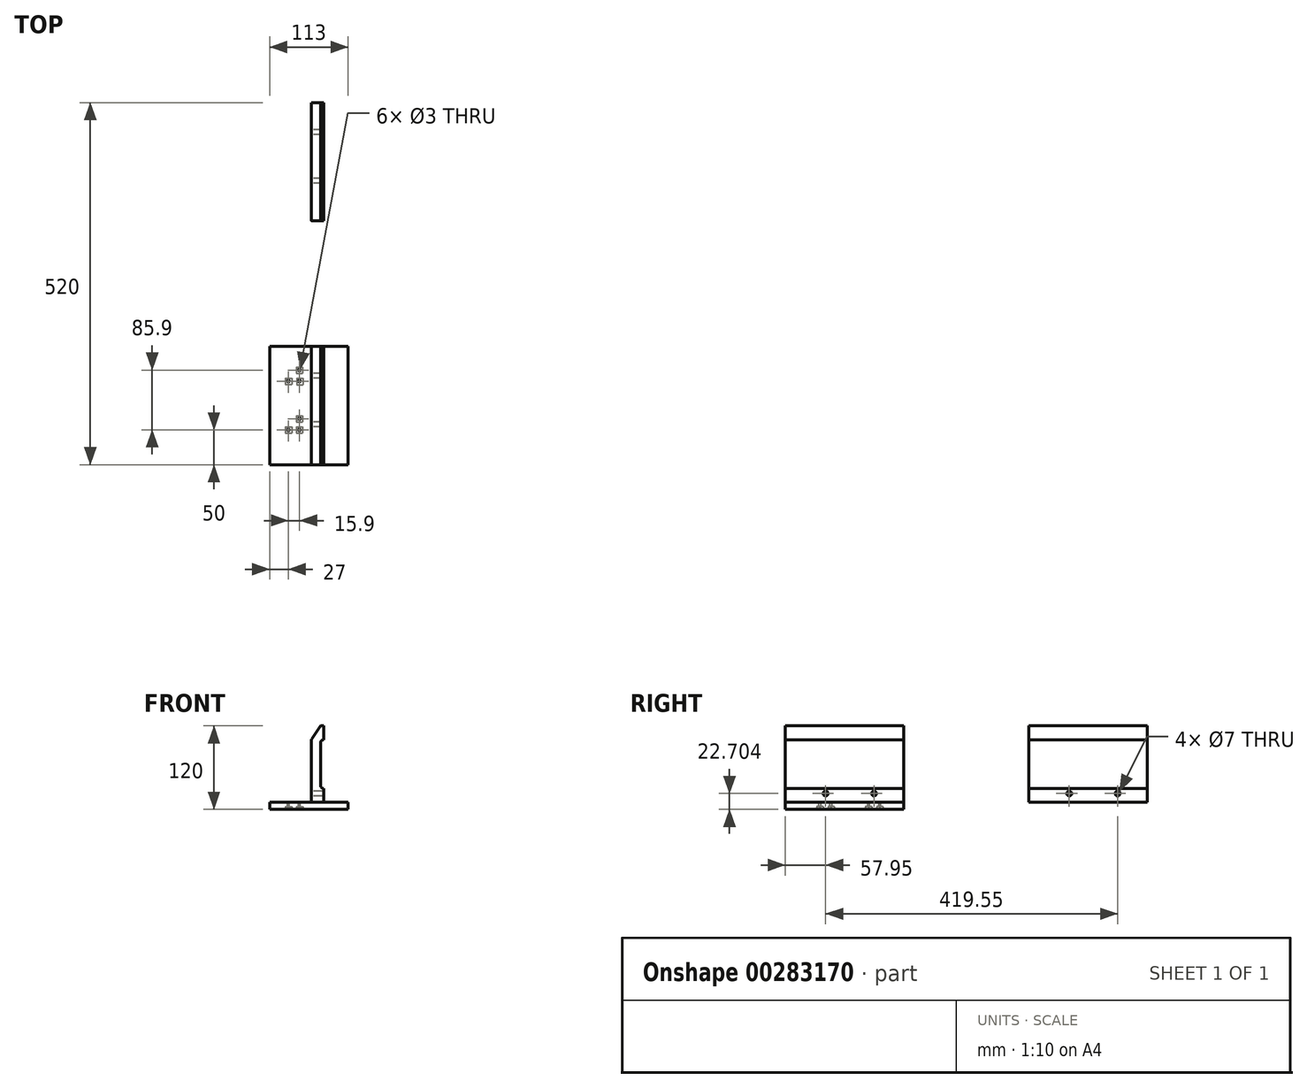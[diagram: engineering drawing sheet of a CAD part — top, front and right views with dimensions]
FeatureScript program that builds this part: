
annotation { "Feature Type Name" : "Feature", "Feature Type Description" : "" }
export const myFeature = defineFeature(function(context is Context, id is Id, definition is map)
    precondition{}
    {
        {
            var Q0;
            Q0=qCreatedBy(makeId("Front.planeOp"),FACE);
            var sketch = newSketch(context, id + "F0", { "sketchPlane" : qUnion([Q0])});
            skLineSegment(sketch, "E0.0", {"start": v(0, -38.38) * mm, "end": v(18, -38.38) * mm});
            skLineSegment(sketch, "E1", {"start": v(18, -38.38) * mm, "end": v(53, -38.38) * mm});
            skLineSegment(sketch, "E2", {"start": v(53, -38.38) * mm, "end": v(53, -48.38) * mm});
            skLineSegment(sketch, "E3", {"start": v(53, -48.38) * mm, "end": v(-60, -48.38) * mm});
            skLineSegment(sketch, "E4", {"start": v(-60, -48.38) * mm, "end": v(-60, -38.38) * mm});
            skLineSegment(sketch, "E5", {"start": v(-60, -38.38) * mm, "end": v(0, -38.38) * mm});
            skSolve(sketch);
        }
        {
            var Q0;
            Q0=qCreatedBy(makeId("Front.planeOp"),FACE);
            var sketch = newSketch(context, id + "F1", { "sketchPlane" : qUnion([Q0])});
            skLineSegment(sketch, "E6", {"start": v(18, 71.62) * mm, "end": v(13, 71.62) * mm});
            skLineSegment(sketch, "E7", {"start": v(13, 71.62) * mm, "end": v(0.8, 52.87) * mm});
            skLineSegment(sketch, "E8", {"start": v(0, 50.14) * mm, "end": v(0, -38.38) * mm});
            skLineSegment(sketch, "E9", {"start": v(0, -38.38) * mm, "end": v(18, -38.38) * mm});
            skLineSegment(sketch, "E10", {"start": v(18, -38.38) * mm, "end": v(18, -18.38) * mm});
            skLineSegment(sketch, "E11", {"start": v(18, -18.38) * mm, "end": v(18, -18.38) * mm});
            skLineSegment(sketch, "E12", {"start": v(13, -13.38) * mm, "end": v(13, 46.62) * mm});
            skLineSegment(sketch, "E13", {"start": v(18, 51.62) * mm, "end": v(18, 51.62) * mm});
            skLineSegment(sketch, "E14", {"start": v(18, 51.62) * mm, "end": v(18, 71.62) * mm});
            skPoint(sketch, "E15.visualSharp", {"position": v(13, 51.62) * mm});
            skArc(sketch, "E15.filletArc", {"start": v(18, 51.62) * mm, "mid": v(14.46, 50.16) * mm, "end": v(13, 46.62) * mm});
            skPoint(sketch, "E16.visualSharp", {"position": v(13, -18.38) * mm});
            skArc(sketch, "E16.filletArc", {"start": v(13, -13.38) * mm, "mid": v(14.46, -16.91) * mm, "end": v(18, -18.38) * mm});
            skPoint(sketch, "E17.visualSharp", {"position": v(0, 51.62) * mm});
            skArc(sketch, "E17.filletArc", {"start": v(0.8, 52.87) * mm, "mid": v(0.2, 51.56) * mm, "end": v(0, 50.14) * mm});
            skSolve(sketch);
        }
        {
            var Q0;
            Q0=makeQuery(id+"F1.imprint","IMPRINT",FACE,{"disambiguationData":[TD([[makeQuery(id+"F1.imprint","IMPRINT",EDGE,{"derivedFrom":sQuery(id+"F1.wireOp",EDGE,"E6")}),1.0]])]});
            var Q1;
            Q1=makeQuery(id+"F0.imprint","IMPRINT",FACE,{"disambiguationData":[TD([[makeQuery(id+"F0.imprint","IMPRINT",EDGE,{"derivedFrom":sQuery(id+"F0.wireOp",EDGE,"E0.0")}),-1.0]])]});
            extrude(context, id + "F2", {"entities" : qUnion([Q0, Q1]), "oppositeDirection" : true, "depth" : 170 * mm});
        }
        {
            var Q0;
            Q0=makeQuery(id+"F2.opExtrude","SWEPT_FACE",FACE,{"disambiguationData":[OSD([sQuery(id+"F0.wireOp",EDGE,"E0.0"),sQuery(id+"F0.wireOp",EDGE,"E1"),sQuery(id+"F0.wireOp",EDGE,"E5")])]});
            var sketch = newSketch(context, id + "F3", { "sketchPlane" : qUnion([Q0])});
            skSolve(sketch);
        }
        {
            var Q0;
            {var subQ0=sQuery(id+"F0.wireOp",EDGE,"E1");Q0=makeQuery(id+"F3.imprint","IMPRINT",FACE,{"disambiguationData":[TD([[makeQuery(id+"F3.imprint","IMPRINT",EDGE,{"derivedFrom":makeQuery(id+"F2.opExtrude","SWEPT_EDGE",EDGE,{"disambiguationData":[OSD([subQ0,sQuery(id+"F0.wireOp",EDGE,"E2")])]})}),-1.0]])]});}
            var sketch = newSketch(context, id + "F4", { "sketchPlane" : qUnion([Q0])});
            skCircle(sketch, "E18", {"center": v(-33, 50) * mm, "radius": 1.5 * mm});
            skCircle(sketch, "E19", {"center": v(-17.1, 50) * mm, "radius": 1.5 * mm});
            skCircle(sketch, "E20", {"center": v(-17.1, 65.9) * mm, "radius": 1.5 * mm});
            skCircle(sketch, "E21", {"center": v(-33, 120) * mm, "radius": 1.5 * mm});
            skCircle(sketch, "E22", {"center": v(-17.1, 120) * mm, "radius": 1.5 * mm});
            skCircle(sketch, "E23", {"center": v(-17.1, 135.9) * mm, "radius": 1.5 * mm});
            skSolve(sketch);
        }
        {
            var Q0;
            Q0=makeQuery(id+"F4.imprint","IMPRINT",FACE,{"disambiguationData":[TD([[makeQuery(id+"F4.imprint","IMPRINT",EDGE,{"derivedFrom":sQuery(id+"F4.wireOp",EDGE,"E22")}),1.0]])]});
            var Q1;
            Q1=makeQuery(id+"F4.imprint","IMPRINT",FACE,{"disambiguationData":[TD([[makeQuery(id+"F4.imprint","IMPRINT",EDGE,{"derivedFrom":sQuery(id+"F4.wireOp",EDGE,"E21")}),1.0]])]});
            var Q2;
            Q2=makeQuery(id+"F4.imprint","IMPRINT",FACE,{"disambiguationData":[TD([[makeQuery(id+"F4.imprint","IMPRINT",EDGE,{"derivedFrom":sQuery(id+"F4.wireOp",EDGE,"E23")}),1.0]])]});
            var Q3;
            Q3=makeQuery(id+"F4.imprint","IMPRINT",FACE,{"disambiguationData":[TD([[makeQuery(id+"F4.imprint","IMPRINT",EDGE,{"derivedFrom":sQuery(id+"F4.wireOp",EDGE,"E20")}),1.0]])]});
            var Q4;
            Q4=makeQuery(id+"F4.imprint","IMPRINT",FACE,{"disambiguationData":[TD([[makeQuery(id+"F4.imprint","IMPRINT",EDGE,{"derivedFrom":sQuery(id+"F4.wireOp",EDGE,"E19")}),1.0]])]});
            var Q5;
            Q5=makeQuery(id+"F4.imprint","IMPRINT",FACE,{"disambiguationData":[TD([[makeQuery(id+"F4.imprint","IMPRINT",EDGE,{"derivedFrom":sQuery(id+"F4.wireOp",EDGE,"E18")}),1.0]])]});
            var Q6;
            Q6=sQuery(id+"F4.wireOp",EDGE,"E23");
            var Q7;
            Q7=sQuery(id+"F4.wireOp",EDGE,"E22");
            var Q8;
            Q8=sQuery(id+"F4.wireOp",EDGE,"E21");
            var Q9;
            Q9=sQuery(id+"F4.wireOp",EDGE,"E20");
            var Q10;
            Q10=sQuery(id+"F4.wireOp",EDGE,"E19");
            var Q11;
            Q11=sQuery(id+"F4.wireOp",EDGE,"E18");
            extrude(context, id + "F5", {"entities" : qUnion([Q0, Q1, Q2, Q3, Q4, Q5]), "operationType" : NewBodyOperationType.REMOVE, "surfaceEntities" : qUnion([Q6, Q7, Q8, Q9, Q10, Q11]), "endBound" : BoundingType.THROUGH_ALL, "oppositeDirection" : true, "depth" : 25 * mm});
        }
        {
            var Q0;
            Q0=makeQuery(id+"F2.opExtrude","SWEPT_FACE",FACE,{"disambiguationData":[OSD([sQuery(id+"F1.wireOp",EDGE,"E8")])]});
            var sketch = newSketch(context, id + "F6", { "sketchPlane" : qUnion([Q0])});
            skCircle(sketch, "E24", {"center": v(-57.95, -25.68) * mm, "radius": 3.5 * mm});
            skCircle(sketch, "E25", {"center": v(-127.5, -25.68) * mm, "radius": 3.5 * mm});
            skSolve(sketch);
        }
        {
            var Q0;
            Q0=makeQuery(id+"F6.imprint","IMPRINT",FACE,{"disambiguationData":[TD([[makeQuery(id+"F6.imprint","IMPRINT",EDGE,{"derivedFrom":sQuery(id+"F6.wireOp",EDGE,"E25")}),1.0]])]});
            var Q1;
            Q1=makeQuery(id+"F6.imprint","IMPRINT",FACE,{"disambiguationData":[TD([[makeQuery(id+"F6.imprint","IMPRINT",EDGE,{"derivedFrom":sQuery(id+"F6.wireOp",EDGE,"E24")}),1.0]])]});
            var Q2;
            Q2=sQuery(id+"F6.wireOp",EDGE,"E25");
            var Q3;
            Q3=sQuery(id+"F6.wireOp",EDGE,"E24");
            extrude(context, id + "F7", {"entities" : qUnion([Q0, Q1]), "operationType" : NewBodyOperationType.REMOVE, "surfaceEntities" : qUnion([Q2, Q3]), "endBound" : BoundingType.THROUGH_ALL, "oppositeDirection" : true, "depth" : 25 * mm});
        }
        {
            var Q0;
            Q0=makeQuery(id+"F2.opExtrude","SWEPT_FACE",FACE,{"disambiguationData":[OSD([sQuery(id+"F0.wireOp",EDGE,"E3")])]});
            var sketch = newSketch(context, id + "F8", { "sketchPlane" : qUnion([Q0])});
            skLineSegment(sketch, "E26.bottom", {"start": v(-37.26, -124.46) * mm, "end": v(-28.26, -124.46) * mm});
            skLineSegment(sketch, "E26.top", {"start": v(-37.26, -115.46) * mm, "end": v(-28.26, -115.46) * mm});
            skLineSegment(sketch, "E26.left", {"start": v(-37.26, -124.46) * mm, "end": v(-37.26, -115.46) * mm});
            skLineSegment(sketch, "E26.right", {"start": v(-28.26, -124.46) * mm, "end": v(-28.26, -115.46) * mm});
            skLineSegment(sketch, "E27.bottom", {"start": v(-21.55, -140.13) * mm, "end": v(-12.55, -140.13) * mm});
            skLineSegment(sketch, "E27.top", {"start": v(-21.55, -131.13) * mm, "end": v(-12.55, -131.13) * mm});
            skLineSegment(sketch, "E27.left", {"start": v(-21.55, -140.13) * mm, "end": v(-21.55, -131.13) * mm});
            skLineSegment(sketch, "E27.right", {"start": v(-12.55, -140.13) * mm, "end": v(-12.55, -131.13) * mm});
            skLineSegment(sketch, "E28.bottom", {"start": v(-21.07, -123.97) * mm, "end": v(-12.07, -123.97) * mm});
            skLineSegment(sketch, "E28.top", {"start": v(-21.07, -114.97) * mm, "end": v(-12.07, -114.97) * mm});
            skLineSegment(sketch, "E28.left", {"start": v(-21.07, -123.97) * mm, "end": v(-21.07, -114.97) * mm});
            skLineSegment(sketch, "E28.right", {"start": v(-12.07, -123.97) * mm, "end": v(-12.07, -114.97) * mm});
            skLineSegment(sketch, "E29.bottom", {"start": v(-21.79, -70.48) * mm, "end": v(-12.79, -70.48) * mm});
            skLineSegment(sketch, "E29.top", {"start": v(-21.79, -61.48) * mm, "end": v(-12.79, -61.48) * mm});
            skLineSegment(sketch, "E29.left", {"start": v(-21.79, -70.48) * mm, "end": v(-21.79, -61.48) * mm});
            skLineSegment(sketch, "E29.right", {"start": v(-12.79, -70.48) * mm, "end": v(-12.79, -61.48) * mm});
            skLineSegment(sketch, "E30.bottom", {"start": v(-21.79, -54.56) * mm, "end": v(-12.79, -54.56) * mm});
            skLineSegment(sketch, "E30.top", {"start": v(-21.79, -45.56) * mm, "end": v(-12.79, -45.56) * mm});
            skLineSegment(sketch, "E30.left", {"start": v(-21.79, -54.56) * mm, "end": v(-21.79, -45.56) * mm});
            skLineSegment(sketch, "E30.right", {"start": v(-12.79, -54.56) * mm, "end": v(-12.79, -45.56) * mm});
            skLineSegment(sketch, "E31.bottom", {"start": v(-37.24, -54.32) * mm, "end": v(-28.24, -54.32) * mm});
            skLineSegment(sketch, "E31.top", {"start": v(-37.24, -45.32) * mm, "end": v(-28.24, -45.32) * mm});
            skLineSegment(sketch, "E31.left", {"start": v(-37.24, -54.32) * mm, "end": v(-37.24, -45.32) * mm});
            skLineSegment(sketch, "E31.right", {"start": v(-28.24, -54.32) * mm, "end": v(-28.24, -45.32) * mm});
            skSolve(sketch);
        }
        {
            var Q0;
            Q0=makeQuery(id+"F8.imprint","IMPRINT",FACE,{"disambiguationData":[TD([[makeQuery(id+"F8.imprint","IMPRINT",EDGE,{"derivedFrom":sQuery(id+"F8.wireOp",EDGE,"E27.bottom")}),1.0]])]});
            var Q1;
            Q1=makeQuery(id+"F8.imprint","IMPRINT",FACE,{"disambiguationData":[TD([[makeQuery(id+"F8.imprint","IMPRINT",EDGE,{"derivedFrom":sQuery(id+"F8.wireOp",EDGE,"E26.bottom")}),1.0]])]});
            var Q2;
            Q2=makeQuery(id+"F8.imprint","IMPRINT",FACE,{"disambiguationData":[TD([[makeQuery(id+"F8.imprint","IMPRINT",EDGE,{"derivedFrom":sQuery(id+"F8.wireOp",EDGE,"E28.bottom")}),1.0]])]});
            var Q3;
            Q3=makeQuery(id+"F8.imprint","IMPRINT",FACE,{"disambiguationData":[TD([[makeQuery(id+"F8.imprint","IMPRINT",EDGE,{"derivedFrom":sQuery(id+"F8.wireOp",EDGE,"E29.bottom")}),1.0]])]});
            var Q4;
            Q4=makeQuery(id+"F8.imprint","IMPRINT",FACE,{"disambiguationData":[TD([[makeQuery(id+"F8.imprint","IMPRINT",EDGE,{"derivedFrom":sQuery(id+"F8.wireOp",EDGE,"E31.bottom")}),1.0]])]});
            var Q5;
            Q5=makeQuery(id+"F8.imprint","IMPRINT",FACE,{"disambiguationData":[TD([[makeQuery(id+"F8.imprint","IMPRINT",EDGE,{"derivedFrom":sQuery(id+"F8.wireOp",EDGE,"E30.bottom")}),1.0]])]});
            var Q6;
            Q6=sQuery(id+"F8.wireOp",EDGE,"E27.left");
            var Q7;
            Q7=sQuery(id+"F8.wireOp",EDGE,"E27.bottom");
            var Q8;
            Q8=sQuery(id+"F8.wireOp",EDGE,"E27.right");
            var Q9;
            Q9=sQuery(id+"F8.wireOp",EDGE,"E27.top");
            var Q10;
            Q10=sQuery(id+"F8.wireOp",EDGE,"E28.left");
            var Q11;
            Q11=sQuery(id+"F8.wireOp",EDGE,"E28.bottom");
            var Q12;
            Q12=sQuery(id+"F8.wireOp",EDGE,"E28.right");
            var Q13;
            Q13=sQuery(id+"F8.wireOp",EDGE,"E28.top");
            var Q14;
            Q14=sQuery(id+"F8.wireOp",EDGE,"E26.left");
            var Q15;
            Q15=sQuery(id+"F8.wireOp",EDGE,"E26.bottom");
            var Q16;
            Q16=sQuery(id+"F8.wireOp",EDGE,"E26.right");
            var Q17;
            Q17=sQuery(id+"F8.wireOp",EDGE,"E26.top");
            var Q18;
            Q18=sQuery(id+"F8.wireOp",EDGE,"E31.left");
            var Q19;
            Q19=sQuery(id+"F8.wireOp",EDGE,"E31.top");
            var Q20;
            Q20=sQuery(id+"F8.wireOp",EDGE,"E31.bottom");
            var Q21;
            Q21=sQuery(id+"F8.wireOp",EDGE,"E31.right");
            var Q22;
            Q22=sQuery(id+"F8.wireOp",EDGE,"E30.left");
            var Q23;
            Q23=sQuery(id+"F8.wireOp",EDGE,"E30.bottom");
            var Q24;
            Q24=sQuery(id+"F8.wireOp",EDGE,"E30.right");
            var Q25;
            Q25=sQuery(id+"F8.wireOp",EDGE,"E30.top");
            var Q26;
            Q26=sQuery(id+"F8.wireOp",EDGE,"E29.left");
            var Q27;
            Q27=sQuery(id+"F8.wireOp",EDGE,"E29.top");
            var Q28;
            Q28=sQuery(id+"F8.wireOp",EDGE,"E29.bottom");
            var Q29;
            Q29=sQuery(id+"F8.wireOp",EDGE,"E29.right");
            extrude(context, id + "F9", {"entities" : qUnion([Q0, Q1, Q2, Q3, Q4, Q5]), "operationType" : NewBodyOperationType.REMOVE, "surfaceEntities" : qUnion([Q6, Q7, Q8, Q9, Q10, Q11, Q12, Q13, Q14, Q15, Q16, Q17, Q18, Q19, Q20, Q21, Q22, Q23, Q24, Q25, Q26, Q27, Q28, Q29]), "oppositeDirection" : true, "depth" : 4 * mm});
        }
        {
            var Q0;
            Q0=makeQuery(id+"F2.opExtrude","SWEPT_BODY",BODY,{"disambiguationData":[OSD([sQuery(id+"F1.wireOp",EDGE,"E6"),sQuery(id+"F1.wireOp",EDGE,"E7"),sQuery(id+"F1.wireOp",EDGE,"E8"),sQuery(id+"F1.wireOp",EDGE,"E9"),sQuery(id+"F1.wireOp",EDGE,"E10"),sQuery(id+"F1.wireOp",EDGE,"E12"),sQuery(id+"F1.wireOp",EDGE,"E14"),sQuery(id+"F1.wireOp",EDGE,"E15.filletArc"),sQuery(id+"F1.wireOp",EDGE,"E16.filletArc"),sQuery(id+"F1.wireOp",EDGE,"E17.filletArc")])]});
            transform(context, id + "F10", {"entities" : qUnion([Q0]), "transformType" : TransformType.TRANSLATION_3D, "dx" : 0 * mm, "dy" : 0 * mm, "dz" : 0 * mm, "makeCopy" : true});
        }
        {
            var Q0;
            Q0=makeQuery(id+"F10.opPattern","COPY",BODY,{"derivedFrom":makeQuery(id+"F2.opExtrude","SWEPT_BODY",BODY,{"disambiguationData":[OSD([sQuery(id+"F1.wireOp",EDGE,"E6"),sQuery(id+"F1.wireOp",EDGE,"E7"),sQuery(id+"F1.wireOp",EDGE,"E8"),sQuery(id+"F1.wireOp",EDGE,"E9"),sQuery(id+"F1.wireOp",EDGE,"E10"),sQuery(id+"F1.wireOp",EDGE,"E12"),sQuery(id+"F1.wireOp",EDGE,"E14"),sQuery(id+"F1.wireOp",EDGE,"E15.filletArc"),sQuery(id+"F1.wireOp",EDGE,"E16.filletArc"),sQuery(id+"F1.wireOp",EDGE,"E17.filletArc")])]}),"instanceName":"1"});
            deleteBodies(context, id + "F11", {"entities" : qUnion([Q0])});
        }
        {
            var Q0;
            Q0=makeQuery(id+"F2.opExtrude","SWEPT_BODY",BODY,{"disambiguationData":[OSD([sQuery(id+"F1.wireOp",EDGE,"E6"),sQuery(id+"F1.wireOp",EDGE,"E7"),sQuery(id+"F1.wireOp",EDGE,"E8"),sQuery(id+"F1.wireOp",EDGE,"E9"),sQuery(id+"F1.wireOp",EDGE,"E10"),sQuery(id+"F1.wireOp",EDGE,"E12"),sQuery(id+"F1.wireOp",EDGE,"E14"),sQuery(id+"F1.wireOp",EDGE,"E15.filletArc"),sQuery(id+"F1.wireOp",EDGE,"E16.filletArc"),sQuery(id+"F1.wireOp",EDGE,"E17.filletArc")])]});
            transform(context, id + "F12", {"entities" : qUnion([Q0]), "transformType" : TransformType.TRANSLATION_3D, "dx" : 0 * mm, "dy" : 350 * mm, "dz" : 0 * mm, "makeCopy" : true});
        }
    });
